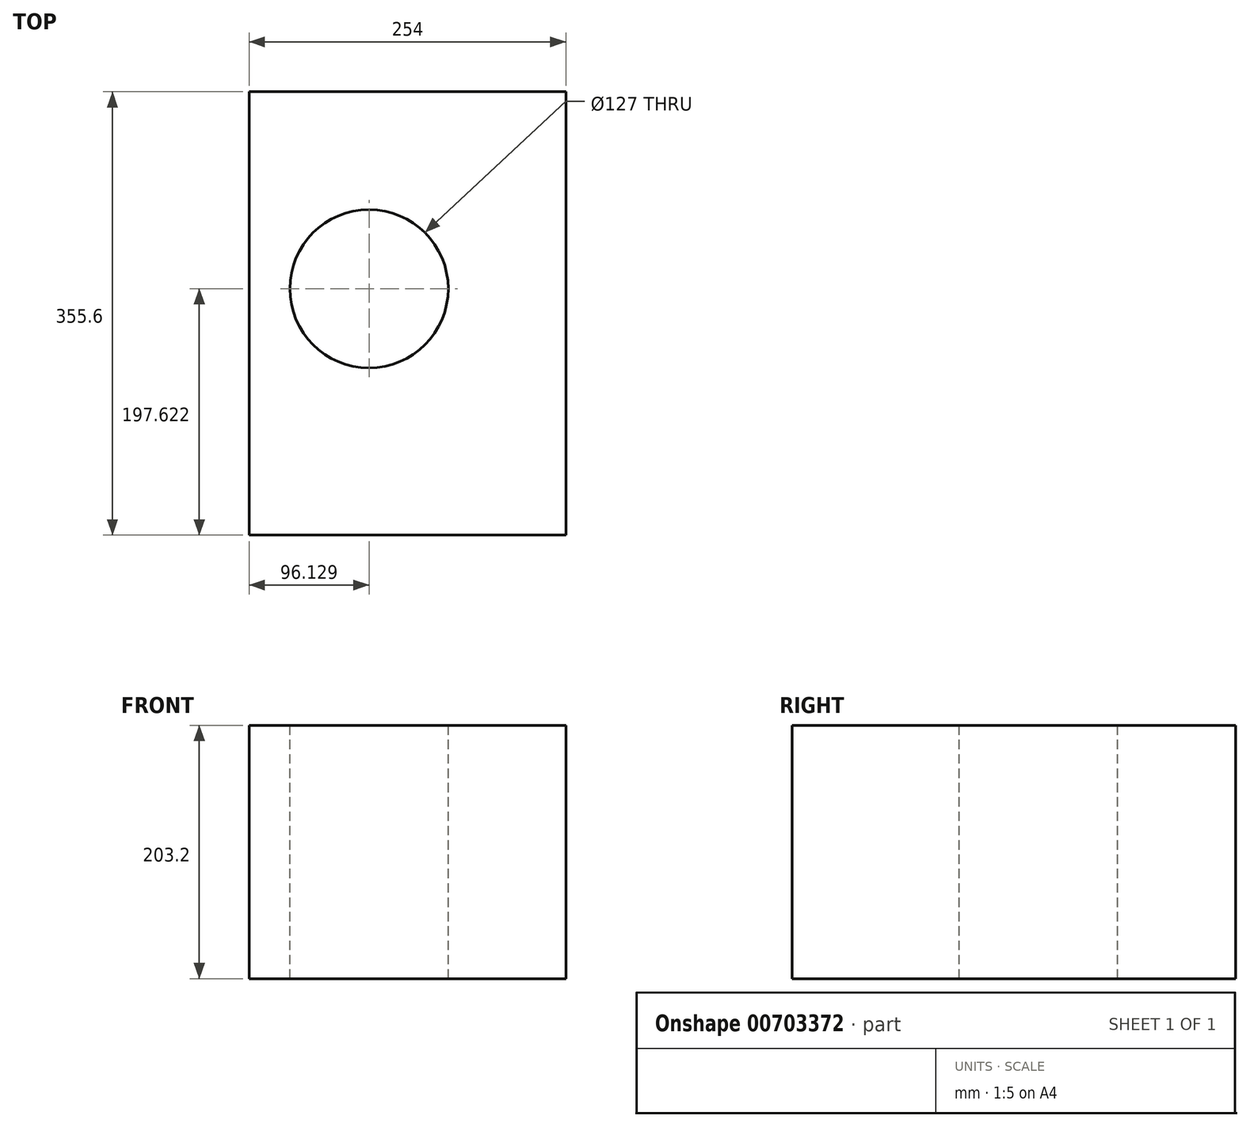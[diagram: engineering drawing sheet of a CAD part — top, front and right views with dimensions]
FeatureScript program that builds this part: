
annotation { "Feature Type Name" : "Feature", "Feature Type Description" : "" }
export const myFeature = defineFeature(function(context is Context, id is Id, definition is map)
    precondition{}
    {
        {
            var Q0;
            Q0=qCreatedBy(makeId("Front.planeOp"),FACE);
            var sketch = newSketch(context, id + "F0", { "sketchPlane" : qUnion([Q0])});
            skLineSegment(sketch, "E0.bottom", {"start": v(-133.11, -102.25) * mm, "end": v(120.89, -102.25) * mm});
            skLineSegment(sketch, "E0.top", {"start": v(-133.11, 100.95) * mm, "end": v(120.89, 100.95) * mm});
            skLineSegment(sketch, "E0.left", {"start": v(-133.11, -102.25) * mm, "end": v(-133.11, 100.95) * mm});
            skLineSegment(sketch, "E0.right", {"start": v(120.89, -102.25) * mm, "end": v(120.89, 100.95) * mm});
            skSolve(sketch);
        }
        {
            var Q0;
            Q0=makeQuery(id+"F0.imprint","IMPRINT",FACE,{"disambiguationData":[TD([[makeQuery(id+"F0.imprint","IMPRINT",EDGE,{"derivedFrom":sQuery(id+"F0.wireOp",EDGE,"E0.bottom")}),1.0]])]});
            extrude(context, id + "F1", {"entities" : qUnion([Q0]), "depth" : 355.6 * mm, "offsetDistance" : 25.4 * mm});
        }
        {
            var Q0;
            Q0=makeQuery(id+"F1.opExtrude","SWEPT_FACE",FACE,{"disambiguationData":[OSD([sQuery(id+"F0.wireOp",EDGE,"E0.top")])]});
            var sketch = newSketch(context, id + "F2", { "sketchPlane" : qUnion([Q0])});
            skCircle(sketch, "E1", {"center": v(-36.98, -157.98) * mm, "radius": 72.9 * mm});
            skSolve(sketch);
        }
        {
            var Q0;
            Q0=sQuery(id+"F2.wireOp",VERTEX,"E1.center");
            var Q1;
            Q1=makeQuery(id+"F1.opExtrude","SWEPT_BODY",BODY,{"disambiguationData":[OSD([sQuery(id+"F0.wireOp",EDGE,"E0.bottom"),sQuery(id+"F0.wireOp",EDGE,"E0.top"),sQuery(id+"F0.wireOp",EDGE,"E0.left"),sQuery(id+"F0.wireOp",EDGE,"E0.right")])]});
            hole(context, id + "F3", {"style" : HoleStyle.SIMPLE, "endStyle" : HoleEndStyle.BLIND, "holeDiameter" : 127 * mm, "majorDiameter" : 6.35 * mm, "holeDepth" : 355.6 * mm, "isTappedThrough" : true, "tappedDepth" : 12.7 * mm, "tapClearance" : 3, "locations" : qUnion([Q0]), "scope" : qUnion([Q1])});
        }
    });
